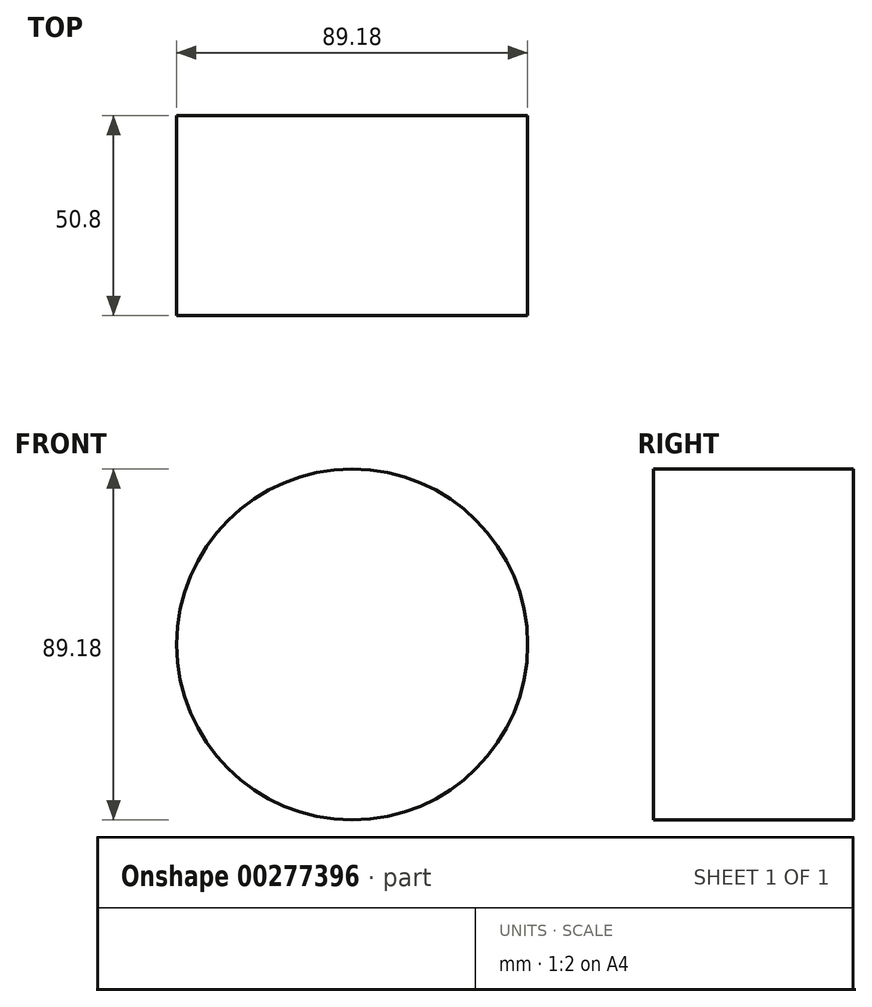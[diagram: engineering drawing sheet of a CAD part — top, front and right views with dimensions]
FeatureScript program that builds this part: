
annotation { "Feature Type Name" : "Feature", "Feature Type Description" : "" }
export const myFeature = defineFeature(function(context is Context, id is Id, definition is map)
    precondition{}
    {
        {
            var Q0;
            Q0=qCreatedBy(makeId("Front.planeOp"),FACE);
            var sketch = newSketch(context, id + "F0", { "sketchPlane" : qUnion([Q0])});
            skCircle(sketch, "E0", {"center": v(0, 0) * mm, "radius": 44.59 * mm});
            skSolve(sketch);
        }
        {
            var Q0;
            Q0=makeQuery(id+"F0.imprint","IMPRINT",FACE,{"disambiguationData":[TD([[makeQuery(id+"F0.imprint","IMPRINT",EDGE,{"derivedFrom":sQuery(id+"F0.wireOp",EDGE,"E0")}),1.0]])]});
            extrude(context, id + "F1", {"entities" : qUnion([Q0]), "depth" : 50.8 * mm});
        }
    });
